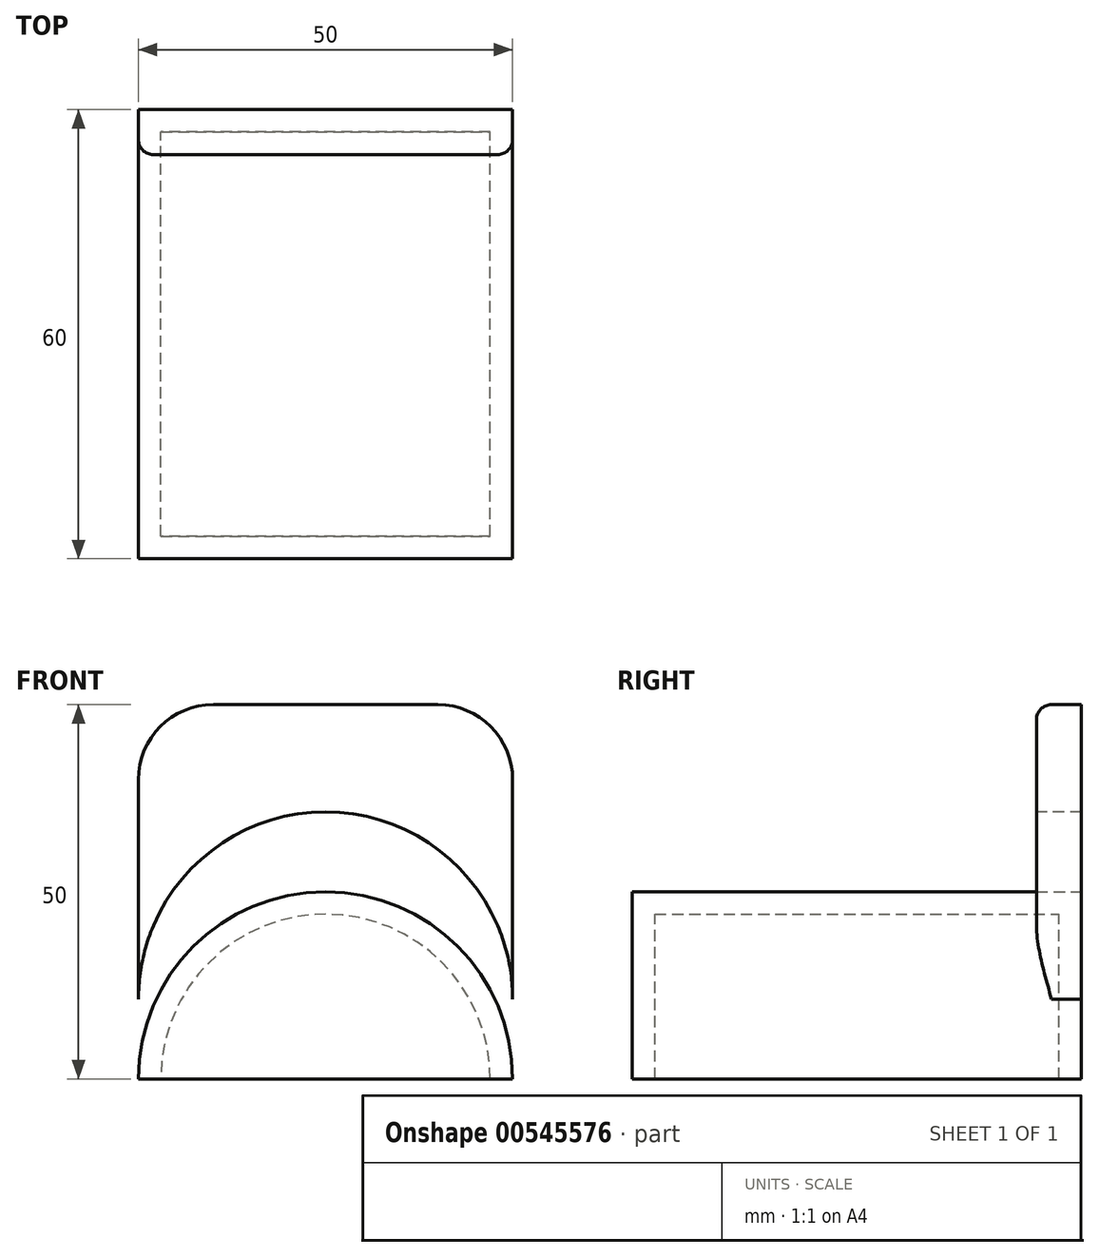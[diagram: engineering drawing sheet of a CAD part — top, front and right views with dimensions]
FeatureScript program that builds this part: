
annotation { "Feature Type Name" : "Feature", "Feature Type Description" : "" }
export const myFeature = defineFeature(function(context is Context, id is Id, definition is map)
    precondition{}
    {
        {
            var Q0;
            Q0=qCreatedBy(makeId("Front.planeOp"),FACE);
            var sketch = newSketch(context, id + "F0", { "sketchPlane" : qUnion([Q0])});
            skCircle(sketch, "E0", {"center": v(0, 0) * mm, "radius": 25 * mm});
            skLineSegment(sketch, "E1.bottom", {"start": v(-25, 0) * mm, "end": v(25, 0) * mm});
            skLineSegment(sketch, "E1.left", {"start": v(-25, 0) * mm, "end": v(-25, 31.87) * mm});
            skLineSegment(sketch, "E1.right", {"start": v(25, 0) * mm, "end": v(25, 21.35) * mm});
            skPoint(sketch, "E2.visualSharp", {"position": v(-25, 41.87) * mm});
            skPoint(sketch, "E3.visualSharp", {"position": v(25, 38.43) * mm});
            skLineSegment(sketch, "E4.top", {"start": v(-15, 50) * mm, "end": v(15, 50) * mm});
            skLineSegment(sketch, "E4.left", {"start": v(-25, 0) * mm, "end": v(-25, 40) * mm});
            skLineSegment(sketch, "E4.right", {"start": v(25, 0) * mm, "end": v(25, 40) * mm});
            skPoint(sketch, "E5.visualSharp", {"position": v(-25, 50) * mm});
            skArc(sketch, "E5.filletArc", {"start": v(-15, 50) * mm, "mid": v(-22.07, 47.07) * mm, "end": v(-25, 40) * mm});
            skPoint(sketch, "E6.visualSharp", {"position": v(25, 50) * mm});
            skArc(sketch, "E6.filletArc", {"start": v(25, 40) * mm, "mid": v(22.07, 47.07) * mm, "end": v(15, 50) * mm});
            skLineSegment(sketch, "E7", {"start": v(-25, 10.67) * mm, "end": v(-25, 0) * mm});
            skLineSegment(sketch, "E8", {"start": v(25, 0) * mm, "end": v(25, 10.67) * mm});
            skPoint(sketch, "E8.endSnap0", {"position": v(25, 10.67) * mm});
            skArc(sketch, "E9", {"start": v(25, 10.67) * mm, "mid": v(0, 35.67) * mm, "end": v(-25, 10.67) * mm});
            skSolve(sketch);
        }
        {
            var Q0;
            {var subQ0=sQuery(id+"F0.wireOp",EDGE,"E1.bottom");Q0=makeQuery(id+"F0.imprint","IMPRINT",FACE,{"disambiguationData":[TD([[makeQuery(id+"F0.imprint","IMPRINT",EDGE,{"derivedFrom":subQ0}),1.0]])]});}
            extrude(context, id + "F1", {"entities" : qUnion([Q0]), "depth" : 50 * mm, "offsetDistance" : 25 * mm});
        }
        {
            var Q0;
            {var subQ0=sQuery(id+"F0.wireOp",EDGE,"E7");Q0=makeQuery(id+"F0.imprint","IMPRINT",FACE,{"disambiguationData":[TD([[makeQuery(id+"F0.imprint","IMPRINT",EDGE,{"derivedFrom":subQ0}),1.0]])]});}
            var Q1;
            {var subQ0=sQuery(id+"F0.wireOp",EDGE,"E1.bottom");Q1=makeQuery(id+"F0.imprint","IMPRINT",FACE,{"disambiguationData":[TD([[makeQuery(id+"F0.imprint","IMPRINT",EDGE,{"derivedFrom":subQ0}),1.0]])]});}
            extrude(context, id + "F2", {"entities" : qUnion([Q0, Q1]), "operationType" : NewBodyOperationType.ADD, "depth" : 54 * mm, "offsetDistance" : 25 * mm, "hasSecondDirection" : true, "secondDirectionOppositeDirection" : false, "secondDirectionDepth" : 50 * mm});
        }
        {
            var Q0;
            Q0=makeQuery(id+"F0.imprint","IMPRINT",FACE,{"disambiguationData":[TD([[makeQuery(id+"F0.imprint","IMPRINT",EDGE,{"derivedFrom":sQuery(id+"F0.wireOp",EDGE,"E4.top")}),-1.0]])]});
            var Q1;
            {var subQ0=sQuery(id+"F0.wireOp",EDGE,"E7");Q1=makeQuery(id+"F0.imprint","IMPRINT",FACE,{"disambiguationData":[TD([[makeQuery(id+"F0.imprint","IMPRINT",EDGE,{"derivedFrom":subQ0}),1.0]])]});}
            var Q2;
            Q2=makeQuery(id+"F1.opExtrude","CAP_FACE",FACE,{"disambiguationData":[OSD([sQuery(id+"F0.wireOp",EDGE,"E0"),sQuery(id+"F0.wireOp",EDGE,"E1.bottom")])],"isStart":true});
            extrude(context, id + "F3", {"entities" : qUnion([Q0, Q1, Q2]), "operationType" : NewBodyOperationType.ADD, "oppositeDirection" : true, "depth" : 6 * mm, "offsetDistance" : 25 * mm});
        }
        {
            var Q0;
            {var subQ0=sQuery(id+"F0.wireOp",EDGE,"E1.bottom");Q0=makeQuery(id+"F3.boolean.opBoolean","MERGE",FACE,{"derivedFrom":[makeQuery(id+"F2.boolean.opBoolean","MERGE",FACE,{"derivedFrom":[makeQuery(id+"F1.opExtrude","SWEPT_FACE",FACE,{"disambiguationData":[OSD([subQ0])]}),makeQuery(id+"F2.opExtrude","SWEPT_FACE",FACE,{"disambiguationData":[OSD([subQ0])]})]}),makeQuery(id+"F3.opExtrude","SWEPT_FACE",FACE,{"disambiguationData":[OSD([subQ0])]})]});}
            shell(context, id + "F4", {"entities" : qUnion([Q0]), "thickness" : 3 * mm});
        }
        {
            var Q0;
            Q0=sQuery(id+"F0.wireOp",VERTEX,"E5.filletArc.center");
            var Q1;
            Q1=sQuery(id+"F0.wireOp",VERTEX,"E6.filletArc.center");
            var Q2;
            Q2=makeQuery(id+"F1.opExtrude","SWEPT_BODY",BODY,{"disambiguationData":[OSD([sQuery(id+"F0.wireOp",EDGE,"E0"),sQuery(id+"F0.wireOp",EDGE,"E1.bottom")])]});
            hole(context, id + "F5", {"style" : HoleStyle.C_SINK, "endStyle" : HoleEndStyle.THROUGH, "standardTappedOrClearance" : lookupTablePath({ "standard" : "ISO", "fit" : "Normal", "size" : "M4", "type" : "Clearance" }), "standardBlindInLast" : lookupTablePath({ "fit" : "Standard", "standard" : "ISO", "size" : "M4", "type" : "Clearance" }), "holeDiameter" : 4.4 * mm, "cSinkDiameter" : 8.96 * mm, "cSinkAngle" : 90 * degree, "isTappedThrough" : true, "tappedDepth" : 12 * mm, "tapClearance" : 3, "startFromSketch" : true, "locations" : qUnion([Q0, Q1]), "scope" : qUnion([Q2])});
        }
        {
            var Q0;
            Q0=makeQuery(id+"F2.opExtrude","CAP_EDGE",EDGE,{"disambiguationData":[OSD([sQuery(id+"F0.wireOp",EDGE,"E9")])],"isStart":false});
            var Q1;
            Q1=makeQuery(id+"F2.opExtrude","CAP_EDGE",EDGE,{"disambiguationData":[OSD([sQuery(id+"F0.wireOp",EDGE,"E9")])],"isStart":true});
            var Q2;
            Q2=makeQuery(id+"F3.opExtrude","CAP_EDGE",EDGE,{"disambiguationData":[OSD([sQuery(id+"F0.wireOp",EDGE,"E4.top")])],"isStart":true});
            fillet(context, id + "F6", {"entities" : qUnion([Q0, Q1, Q2]), "radius" : 2 * mm, "tangentPropagation" : true, "allowEdgeOverflow" : false});
        }
    });
